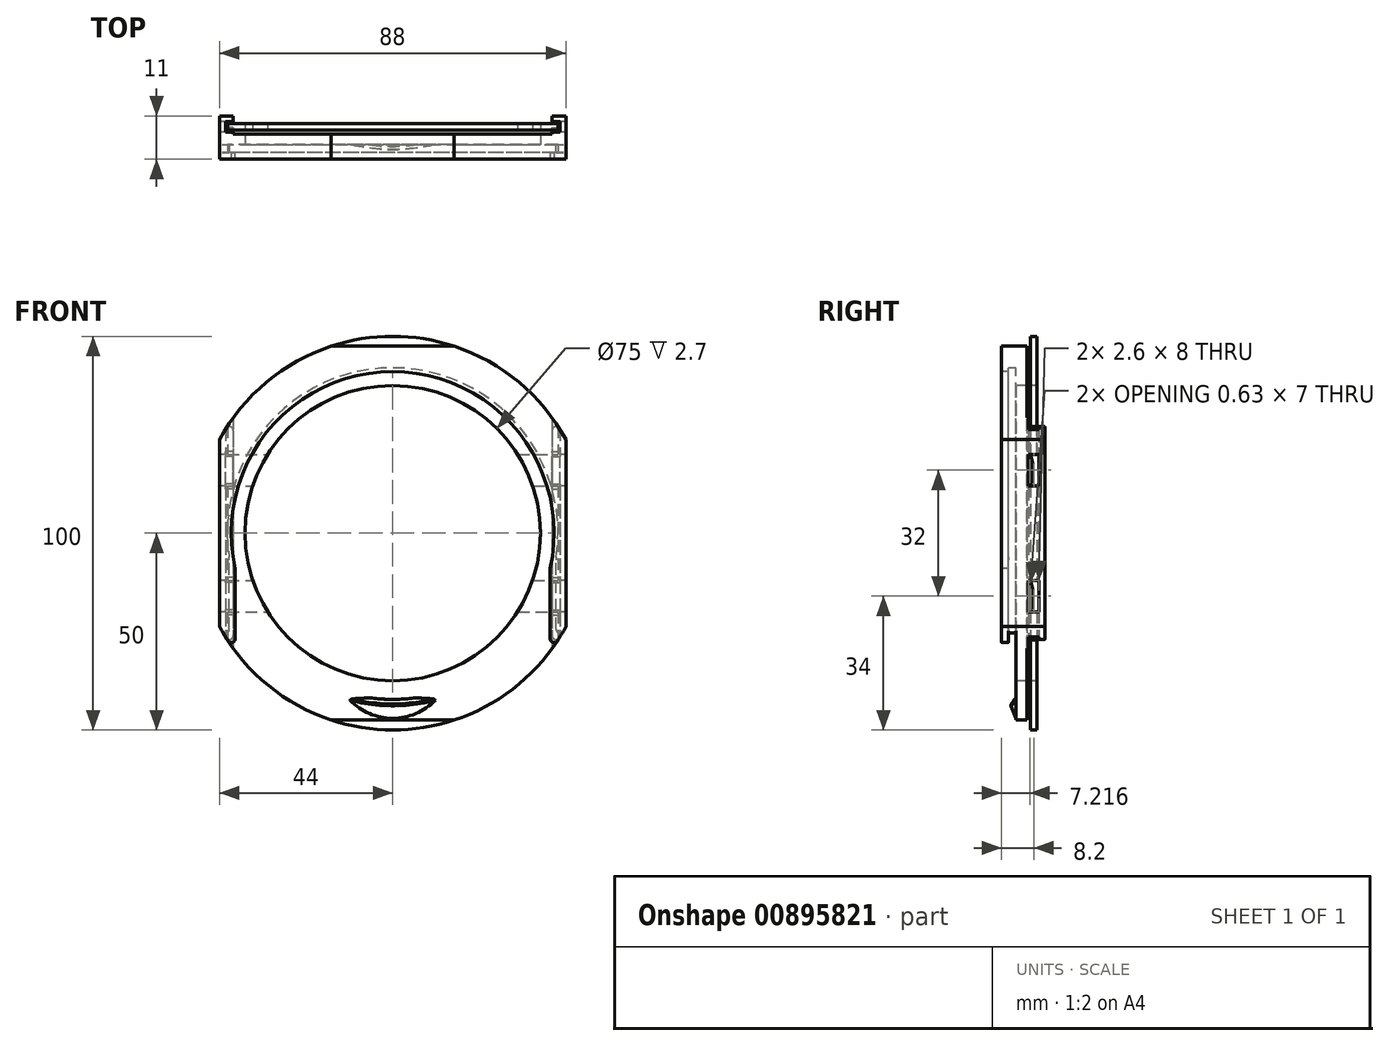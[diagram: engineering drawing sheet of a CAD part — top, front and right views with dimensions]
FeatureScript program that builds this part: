
annotation { "Feature Type Name" : "Feature", "Feature Type Description" : "" }
export const myFeature = defineFeature(function(context is Context, id is Id, definition is map)
    precondition{}
    {
        {
            var Q0;
            Q0=qCreatedBy(makeId("Front.planeOp"),FACE);
            var sketch = newSketch(context, id + "F0", { "sketchPlane" : qUnion([Q0])});
            skLineSegment(sketch, "E0.bottom", {"start": v(42, 50) * mm, "end": v(-42, 50) * mm});
            skLineSegment(sketch, "E0.top", {"start": v(42, -50) * mm, "end": v(-42, -50) * mm});
            skLineSegment(sketch, "E0.left", {"start": v(42, 50) * mm, "end": v(42, -50) * mm});
            skLineSegment(sketch, "E0.right", {"start": v(-42, 50) * mm, "end": v(-42, -50) * mm});
            skPoint(sketch, "E0.middle", {"position": v(0, 0) * mm});
            skSolve(sketch);
        }
        {
            var Q0;
            Q0=makeQuery(id+"F0.imprint","IMPRINT",FACE,{"disambiguationData":[TD([[makeQuery(id+"F0.imprint","IMPRINT",EDGE,{"derivedFrom":sQuery(id+"F0.wireOp",EDGE,"E0.bottom")}),1.0]])]});
            extrude(context, id + "F1", {"entities" : qUnion([Q0]), "depth" : .8 * mm, "offsetDistance" : 25 * mm, "hasSecondDirection" : true, "secondDirectionOppositeDirection" : true, "secondDirectionDepth" : .8 * mm});
        }
        {
            var Q0;
            Q0=qCreatedBy(makeId("Top.planeOp"),FACE);
            var sketch = newSketch(context, id + "F2", { "sketchPlane" : qUnion([Q0])});
            skLineSegment(sketch, "E1.0", {"start": v(42, 0.8) * mm, "end": v(-42, 0.8) * mm, "construction": true});
            skLineSegment(sketch, "E2.0", {"start": v(-42, -0.8) * mm, "end": v(-42, 0.8) * mm, "construction": true});
            skLineSegment(sketch, "E3.0", {"start": v(42, -0.8) * mm, "end": v(-42, -0.8) * mm, "construction": true});
            skLineSegment(sketch, "E4.0", {"start": v(42, -0.8) * mm, "end": v(42, 0.8) * mm, "construction": true});
            skLineSegment(sketch, "E5", {"start": v(-42.5, 1.3) * mm, "end": v(-42.5, -1.3) * mm});
            skLineSegment(sketch, "E6", {"start": v(-42.5, 1.3) * mm, "end": v(-40.5, 1.3) * mm});
            skLineSegment(sketch, "E7.MirrorCS", {"start": v(42.5, 1.3) * mm, "end": v(42.5, -1.3) * mm});
            skLineSegment(sketch, "E8.MirrorCS", {"start": v(42.5, 1.3) * mm, "end": v(40.5, 1.3) * mm});
            skLineSegment(sketch, "E9", {"start": v(-40.5, 1.3) * mm, "end": v(-40.5, 2.8) * mm});
            skLineSegment(sketch, "E10", {"start": v(-40.5, 2.8) * mm, "end": v(-44, 2.8) * mm});
            skLineSegment(sketch, "E11", {"start": v(-44, 2.8) * mm, "end": v(-44, -8.2) * mm});
            skLineSegment(sketch, "E12.MirrorCS", {"start": v(40.5, 1.3) * mm, "end": v(40.5, 2.8) * mm});
            skLineSegment(sketch, "E13.MirrorCS", {"start": v(40.5, 2.8) * mm, "end": v(44, 2.8) * mm});
            skLineSegment(sketch, "E14.MirrorCS", {"start": v(44, 2.8) * mm, "end": v(44, -8.2) * mm});
            skLineSegment(sketch, "E15", {"start": v(-44, -8.2) * mm, "end": v(44, -8.2) * mm});
            skLineSegment(sketch, "E16", {"start": v(-42.5, -1.3) * mm, "end": v(-40.5, -1.3) * mm});
            skLineSegment(sketch, "E17", {"start": v(-40.5, -1.3) * mm, "end": v(-40.5, -1.8) * mm});
            skLineSegment(sketch, "E18.MirrorCS", {"start": v(42.5, -1.3) * mm, "end": v(40.5, -1.3) * mm});
            skLineSegment(sketch, "E19.MirrorCS", {"start": v(40.5, -1.3) * mm, "end": v(40.5, -1.8) * mm});
            skLineSegment(sketch, "E20", {"start": v(40.5, -1.8) * mm, "end": v(-40.5, -1.8) * mm});
            skSolve(sketch);
        }
        {
            var Q0;
            Q0=qSketchRegion(id+"F2",true);
            extrude(context, id + "F3", {"entities" : qUnion([Q0]), "endBound" : BoundingType.SYMMETRIC, "depth" : 95 * mm, "offsetDistance" : 25 * mm});
        }
        {
            var Q0;
            Q0=qCreatedBy(makeId("Right.planeOp"),FACE);
            var sketch = newSketch(context, id + "F4", { "sketchPlane" : qUnion([Q0])});
            skLineSegment(sketch, "E21.top", {"start": v(3, 37.5) * mm, "end": v(-4.5, 37.5) * mm});
            skLineSegment(sketch, "E22", {"start": v(-4.5, 37.5) * mm, "end": v(-4.5, 42) * mm});
            skLineSegment(sketch, "E23", {"start": v(-4.5, 42) * mm, "end": v(-6.5, 42) * mm});
            skLineSegment(sketch, "E24", {"start": v(-6.5, 42) * mm, "end": v(-6.5, 41) * mm});
            skLineSegment(sketch, "E25", {"start": v(-6.5, 41) * mm, "end": v(-8.5, 41) * mm});
            skLineSegment(sketch, "E26", {"start": v(-8.5, 41) * mm, "end": v(-8.5, 0) * mm});
            skLineSegment(sketch, "E27", {"start": v(3, 37.5) * mm, "end": v(3, 0) * mm});
            skLineSegment(sketch, "E28", {"start": v(3, 0) * mm, "end": v(-8.5, 0) * mm});
            skSolve(sketch);
        }
        {
            var Q0;
            Q0=qSketchRegion(id+"F4",true);
            var Q1;
            Q1=sQuery(id+"F4.wireOp",EDGE,"E28");
            revolve(context, id + "F5", {"operationType" : NewBodyOperationType.REMOVE, "surfaceOperationType" : NewSurfaceOperationType.NEW, "entities" : qUnion([Q0]), "axis" : qUnion([Q1]), "revolveType" : RevolveType.FULL, "oppositeDirection" : true});
        }
        {
            var Q0;
            Q0=makeQuery(id+"F3.opExtrude","SWEPT_FACE",FACE,{"disambiguationData":[OSD([sQuery(id+"F2.wireOp",EDGE,"E15")])]});
            var sketch = newSketch(context, id + "F6", { "sketchPlane" : qUnion([Q0])});
            skLineSegment(sketch, "E29.0.0", {"start": v(-44, -47.5) * mm, "end": v(44, -47.5) * mm, "construction": true});
            skLineSegment(sketch, "E29.0.1", {"start": v(44, -47.5) * mm, "end": v(44, 47.5) * mm, "construction": true});
            skLineSegment(sketch, "E29.0.2", {"start": v(44, 47.5) * mm, "end": v(-44, 47.5) * mm, "construction": true});
            skLineSegment(sketch, "E29.0.3", {"start": v(-44, 47.5) * mm, "end": v(-44, -47.5) * mm, "construction": true});
            skLineSegment(sketch, "E30", {"start": v(-40, -9) * mm, "end": v(-40, -47.5) * mm});
            skLineSegment(sketch, "E31", {"start": v(40, -9) * mm, "end": v(40, -47.5) * mm});
            skArc(sketch, "E32", {"start": v(-40, -9) * mm, "mid": v(0, -41) * mm, "end": v(40, -9) * mm});
            skLineSegment(sketch, "E33", {"start": v(-40, -47.5) * mm, "end": v(40, -47.5) * mm});
            skSolve(sketch);
        }
        {
            var Q0;
            Q0=qSketchRegion(id+"F6",true);
            var Q1;
            Q1=makeQuery(id+"F5.boolean.opBoolean","COPY",FACE,{"derivedFrom":makeQuery(id+"F5.opRevolve","SWEPT_FACE",FACE,{"disambiguationData":[OSD([sQuery(id+"F4.wireOp",EDGE,"E22")])]})});
            extrude(context, id + "F7", {"entities" : qUnion([Q0]), "operationType" : NewBodyOperationType.REMOVE, "endBound" : BoundingType.UP_TO_SURFACE, "oppositeDirection" : true, "depth" : 25 * mm, "endBoundEntityFace" : qUnion([Q1]), "offsetDistance" : 25 * mm});
        }
        {
            var Q0;
            Q0=qCreatedBy(makeId("Front.planeOp"),FACE);
            var sketch = newSketch(context, id + "F8", { "sketchPlane" : qUnion([Q0])});
            skCircle(sketch, "E34", {"center": v(0, 0) * mm, "radius": 50 * mm});
            skCircle(sketch, "E35", {"center": v(0, 0) * mm, "radius": 70 * mm});
            skSolve(sketch);
        }
        {
            var Q0;
            Q0=qSketchRegion(id+"F8",true);
            extrude(context, id + "F9", {"entities" : qUnion([Q0]), "operationType" : NewBodyOperationType.REMOVE, "endBound" : BoundingType.SYMMETRIC, "oppositeDirection" : true, "depth" : 500 * mm, "offsetDistance" : 25 * mm});
        }
        {
            var Q0;
            Q0=qCreatedBy(makeId("Top.planeOp"),FACE);
            var sketch = newSketch(context, id + "F10", { "sketchPlane" : qUnion([Q0])});
            skLineSegment(sketch, "E36", {"start": v(-42, -4.5) * mm, "end": v(-42, -3.5) * mm, "construction": true});
            skLineSegment(sketch, "E37", {"start": v(42, -4.5) * mm, "end": v(42, -6.5) * mm, "construction": true});
            skLineSegment(sketch, "E38.bottom", {"start": v(-41.5, -4.5) * mm, "end": v(41.5, -4.5) * mm});
            skLineSegment(sketch, "E38.left", {"start": v(-41.5, -6.5) * mm, "end": v(-41.5, -4.5) * mm});
            skLineSegment(sketch, "E38.right", {"start": v(41.5, -6.5) * mm, "end": v(41.5, -4.5) * mm});
            skLineSegment(sketch, "E39.0.0", {"start": v(-15.61, -4.5) * mm, "end": v(15.61, -4.5) * mm});
            skLineSegment(sketch, "E39.0.1", {"start": v(15.61, -4.5) * mm, "end": v(40, -4.5) * mm});
            skLineSegment(sketch, "E39.0.3", {"start": v(42, -4.5) * mm, "end": v(-42, -4.5) * mm, "construction": true});
            skLineSegment(sketch, "E39.0.5", {"start": v(-40, -4.5) * mm, "end": v(-15.61, -4.5) * mm});
            skLineSegment(sketch, "E40.0", {"start": v(41, -6.5) * mm, "end": v(-41, -6.5) * mm, "construction": true});
            skLineSegment(sketch, "E41", {"start": v(-41.5, -6.5) * mm, "end": v(41.5, -6.5) * mm});
            skSolve(sketch);
        }
        {
            var Q0;
            Q0=qSketchRegion(id+"F10",true);
            extrude(context, id + "F11", {"entities" : qUnion([Q0]), "operationType" : NewBodyOperationType.REMOVE, "oppositeDirection" : true, "depth" : 50 * mm, "offsetDistance" : 25 * mm});
        }
        {
            var Q0;
            Q0=makeQuery(id+"F11.boolean.opBoolean","INTERSECT",EDGE,{"derivedFrom":[makeQuery(id+"F5.boolean.opBoolean","COPY",FACE,{"derivedFrom":makeQuery(id+"F5.opRevolve","SWEPT_FACE",FACE,{"disambiguationData":[OSD([sQuery(id+"F4.wireOp",EDGE,"E23")])]})}),makeQuery(id+"F11.opExtrude","SWEPT_FACE",FACE,{"disambiguationData":[OSD([sQuery(id+"F10.wireOp",EDGE,"E38.right")])]})]});
            var Q1;
            Q1=makeQuery(id+"F11.boolean.opBoolean","INTERSECT",EDGE,{"derivedFrom":[makeQuery(id+"F5.boolean.opBoolean","COPY",FACE,{"derivedFrom":makeQuery(id+"F5.opRevolve","SWEPT_FACE",FACE,{"disambiguationData":[OSD([sQuery(id+"F4.wireOp",EDGE,"E23")])]})}),makeQuery(id+"F11.opExtrude","SWEPT_FACE",FACE,{"disambiguationData":[OSD([sQuery(id+"F10.wireOp",EDGE,"E38.left")])]})]});
            fillet(context, id + "F12", {"entities" : qUnion([Q0, Q1]), "radius" : 5 * mm, "tangentPropagation" : true, "allowEdgeOverflow" : false});
        }
        {
            var Q0;
            {var subQ0=sQuery(id+"F2.wireOp",EDGE,"E16");var subQ1=sQuery(id+"F2.wireOp",EDGE,"E11");var subQ2=sQuery(id+"F2.wireOp",EDGE,"E10");var subQ3=sQuery(id+"F2.wireOp",EDGE,"E5");var subQ4=sQuery(id+"F2.wireOp",EDGE,"E15");var subQ5=sQuery(id+"F2.wireOp",EDGE,"E20");var subQ6=sQuery(id+"F2.wireOp",EDGE,"E17");var subQ7=sQuery(id+"F2.wireOp",EDGE,"E9");var subQ8=sQuery(id+"F2.wireOp",EDGE,"E6");Q0=makeQuery(id+"F11.boolean.opBoolean","INTERSECT",EDGE,{"derivedFrom":[makeQuery(id+"F9.boolean.opBoolean","COPY",FACE,{"disambiguationData":[TD([makeQuery(id+"F3.opExtrude","SWEPT_FACE",FACE,{"disambiguationData":[OSD([subQ3])]}),makeQuery(id+"F3.opExtrude","CAP_FACE",FACE,{"disambiguationData":[OSD([subQ3,subQ8,sQuery(id+"F2.wireOp",EDGE,"E7.MirrorCS"),sQuery(id+"F2.wireOp",EDGE,"E8.MirrorCS"),subQ7,subQ2,subQ1,sQuery(id+"F2.wireOp",EDGE,"E12.MirrorCS"),sQuery(id+"F2.wireOp",EDGE,"E13.MirrorCS"),sQuery(id+"F2.wireOp",EDGE,"E14.MirrorCS"),subQ4,subQ0,subQ6,sQuery(id+"F2.wireOp",EDGE,"E18.MirrorCS"),sQuery(id+"F2.wireOp",EDGE,"E19.MirrorCS"),subQ5])],"isStart":true}),makeQuery(id+"F3.opExtrude","SWEPT_FACE",FACE,{"disambiguationData":[OSD([subQ8])]}),makeQuery(id+"F3.opExtrude","SWEPT_FACE",FACE,{"disambiguationData":[OSD([subQ7])]}),makeQuery(id+"F3.opExtrude","SWEPT_FACE",FACE,{"disambiguationData":[OSD([subQ2])]}),makeQuery(id+"F3.opExtrude","SWEPT_FACE",FACE,{"disambiguationData":[OSD([subQ1])]}),makeQuery(id+"F3.opExtrude","SWEPT_FACE",FACE,{"disambiguationData":[OSD([subQ4])]}),makeQuery(id+"F3.opExtrude","SWEPT_FACE",FACE,{"disambiguationData":[OSD([subQ0])]}),makeQuery(id+"F3.opExtrude","SWEPT_FACE",FACE,{"disambiguationData":[OSD([subQ6])]}),makeQuery(id+"F3.opExtrude","SWEPT_FACE",FACE,{"disambiguationData":[OSD([subQ5])]}),makeQuery(id+"F5.boolean.opBoolean","COPY",FACE,{"derivedFrom":makeQuery(id+"F5.opRevolve","SWEPT_FACE",FACE,{"disambiguationData":[OSD([sQuery(id+"F4.wireOp",EDGE,"t31NqOFZ-bdFC-osZE-Ytuw-QL428Am0EnsE")])]})}),makeQuery(id+"F7.boolean.opBoolean","COPY",FACE,{"derivedFrom":makeQuery(id+"F7.opExtrude","SWEPT_FACE",FACE,{"disambiguationData":[OSD([sQuery(id+"F6.wireOp",EDGE,"E30")])]})})])],"derivedFrom":makeQuery(id+"F9.opExtrude","SWEPT_FACE",FACE,{"disambiguationData":[OSD([sQuery(id+"F8.wireOp",EDGE,"E34")])]})}),makeQuery(id+"F11.opExtrude","SWEPT_FACE",FACE,{"disambiguationData":[OSD([sQuery(id+"F10.wireOp",EDGE,"E38.left")])]})]});}
            var Q1;
            {var subQ0=sQuery(id+"F2.wireOp",EDGE,"E20");var subQ1=sQuery(id+"F2.wireOp",EDGE,"E14.MirrorCS");var subQ2=sQuery(id+"F2.wireOp",EDGE,"E13.MirrorCS");var subQ3=sQuery(id+"F2.wireOp",EDGE,"E15");var subQ4=sQuery(id+"F2.wireOp",EDGE,"E19.MirrorCS");var subQ5=sQuery(id+"F2.wireOp",EDGE,"E18.MirrorCS");var subQ6=sQuery(id+"F2.wireOp",EDGE,"E12.MirrorCS");var subQ7=sQuery(id+"F2.wireOp",EDGE,"E8.MirrorCS");var subQ8=sQuery(id+"F2.wireOp",EDGE,"E7.MirrorCS");Q1=makeQuery(id+"F11.boolean.opBoolean","INTERSECT",EDGE,{"derivedFrom":[makeQuery(id+"F9.boolean.opBoolean","COPY",FACE,{"disambiguationData":[TD([makeQuery(id+"F3.opExtrude","CAP_FACE",FACE,{"disambiguationData":[OSD([sQuery(id+"F2.wireOp",EDGE,"E5"),sQuery(id+"F2.wireOp",EDGE,"E6"),subQ8,subQ7,sQuery(id+"F2.wireOp",EDGE,"E9"),sQuery(id+"F2.wireOp",EDGE,"E10"),sQuery(id+"F2.wireOp",EDGE,"E11"),subQ6,subQ2,subQ1,subQ3,sQuery(id+"F2.wireOp",EDGE,"E16"),sQuery(id+"F2.wireOp",EDGE,"E17"),subQ5,subQ4,subQ0])],"isStart":true}),makeQuery(id+"F3.opExtrude","SWEPT_FACE",FACE,{"disambiguationData":[OSD([subQ8])]}),makeQuery(id+"F3.opExtrude","SWEPT_FACE",FACE,{"disambiguationData":[OSD([subQ7])]}),makeQuery(id+"F3.opExtrude","SWEPT_FACE",FACE,{"disambiguationData":[OSD([subQ6])]}),makeQuery(id+"F3.opExtrude","SWEPT_FACE",FACE,{"disambiguationData":[OSD([subQ2])]}),makeQuery(id+"F3.opExtrude","SWEPT_FACE",FACE,{"disambiguationData":[OSD([subQ1])]}),makeQuery(id+"F3.opExtrude","SWEPT_FACE",FACE,{"disambiguationData":[OSD([subQ3])]}),makeQuery(id+"F3.opExtrude","SWEPT_FACE",FACE,{"disambiguationData":[OSD([subQ5])]}),makeQuery(id+"F3.opExtrude","SWEPT_FACE",FACE,{"disambiguationData":[OSD([subQ4])]}),makeQuery(id+"F3.opExtrude","SWEPT_FACE",FACE,{"disambiguationData":[OSD([subQ0])]}),makeQuery(id+"F5.boolean.opBoolean","COPY",FACE,{"derivedFrom":makeQuery(id+"F5.opRevolve","SWEPT_FACE",FACE,{"disambiguationData":[OSD([sQuery(id+"F4.wireOp",EDGE,"t31NqOFZ-bdFC-osZE-Ytuw-QL428Am0EnsE")])]})}),makeQuery(id+"F7.boolean.opBoolean","COPY",FACE,{"derivedFrom":makeQuery(id+"F7.opExtrude","SWEPT_FACE",FACE,{"disambiguationData":[OSD([sQuery(id+"F6.wireOp",EDGE,"E31")])]})})])],"derivedFrom":makeQuery(id+"F9.opExtrude","SWEPT_FACE",FACE,{"disambiguationData":[OSD([sQuery(id+"F8.wireOp",EDGE,"E34")])]})}),makeQuery(id+"F11.opExtrude","SWEPT_FACE",FACE,{"disambiguationData":[OSD([sQuery(id+"F10.wireOp",EDGE,"E38.right")])]})]});}
            fillet(context, id + "F13", {"entities" : qUnion([Q0, Q1]), "radius" : 1 * mm, "tangentPropagation" : true, "allowEdgeOverflow" : false});
        }
        {
            var Q0;
            Q0=qCreatedBy(makeId("Right.planeOp"),FACE);
            var sketch = newSketch(context, id + "F14", { "sketchPlane" : qUnion([Q0])});
            skLineSegment(sketch, "E42.0.0", {"start": v(-8.2, 23.75) * mm, "end": v(2.8, 23.75) * mm, "construction": true});
            skLineSegment(sketch, "E42.0.1", {"start": v(2.8, 23.75) * mm, "end": v(2.8, -23.75) * mm, "construction": true});
            skLineSegment(sketch, "E42.0.2", {"start": v(-8.2, -23.75) * mm, "end": v(2.8, -23.75) * mm, "construction": true});
            skLineSegment(sketch, "E42.0.3", {"start": v(-8.2, -23.75) * mm, "end": v(-8.2, 23.75) * mm, "construction": true});
            skLineSegment(sketch, "E43.0", {"start": v(1.3, 26.34) * mm, "end": v(-1.3, 26.34) * mm, "construction": true});
            skLineSegment(sketch, "E44.0", {"start": v(-1.3, -26.34) * mm, "end": v(1.3, -26.34) * mm, "construction": true});
            skLineSegment(sketch, "E45.bottom", {"start": v(1.3, 20) * mm, "end": v(-1.3, 20) * mm});
            skLineSegment(sketch, "E45.top", {"start": v(1.3, 12) * mm, "end": v(-1.3, 12) * mm});
            skLineSegment(sketch, "E45.left", {"start": v(1.3, 20) * mm, "end": v(1.3, 12) * mm});
            skLineSegment(sketch, "E45.right", {"start": v(-1.3, 20) * mm, "end": v(-1.3, 12) * mm});
            skLineSegment(sketch, "E46.MirrorCS", {"start": v(1.3, -20) * mm, "end": v(-1.3, -20) * mm});
            skLineSegment(sketch, "E47.MirrorCS", {"start": v(-1.3, -20) * mm, "end": v(-1.3, -12) * mm});
            skLineSegment(sketch, "E48.MirrorCS", {"start": v(1.3, -12) * mm, "end": v(-1.3, -12) * mm});
            skLineSegment(sketch, "E49.MirrorCS", {"start": v(1.3, -20) * mm, "end": v(1.3, -12) * mm});
            skSolve(sketch);
        }
        {
            var Q0;
            Q0=makeQuery(id+"F14.imprint","IMPRINT",FACE,{"disambiguationData":[TD([[makeQuery(id+"F14.imprint","IMPRINT",EDGE,{"derivedFrom":sQuery(id+"F14.wireOp",EDGE,"E45.bottom")}),1.0]])]});
            var Q1;
            Q1=makeQuery(id+"F14.imprint","IMPRINT",FACE,{"disambiguationData":[TD([[makeQuery(id+"F14.imprint","IMPRINT",EDGE,{"derivedFrom":sQuery(id+"F14.wireOp",EDGE,"E46.MirrorCS")}),-1.0]])]});
            extrude(context, id + "F15", {"entities" : qUnion([Q0, Q1]), "operationType" : NewBodyOperationType.REMOVE, "endBound" : BoundingType.SYMMETRIC, "depth" : 100 * mm, "offsetDistance" : 25 * mm});
        }
        {
            var Q0;
            Q0=makeQuery(id+"F15.boolean.opBoolean","SPLIT",FACE,{"disambiguationData":[TD([makeQuery(id+"F15.opExtrude","SWEPT_FACE",FACE,{"disambiguationData":[OSD([sQuery(id+"F14.wireOp",EDGE,"E45.top")])]})])],"derivedFrom":makeQuery(id+"F3.opExtrude","SWEPT_FACE",FACE,{"disambiguationData":[OSD([sQuery(id+"F2.wireOp",EDGE,"E5")])]})});
            var sketch = newSketch(context, id + "F16", { "sketchPlane" : qUnion([Q0])});
            skLineSegment(sketch, "E50.0", {"start": v(-1.3, 20) * mm, "end": v(1.3, 20) * mm, "construction": true});
            skLineSegment(sketch, "E51.0", {"start": v(-1.3, 12) * mm, "end": v(1.3, 12) * mm, "construction": true});
            skArc(sketch, "E52", {"start": v(-1.3, 12.5) * mm, "mid": v(-0.67, 16) * mm, "end": v(-1.3, 19.5) * mm});
            skLineSegment(sketch, "E53", {"start": v(6.42, 16) * mm, "end": v(-9.93, 16) * mm, "construction": true});
            skArc(sketch, "E54.0", {"start": v(-1.3, 11.26) * mm, "mid": v(-0.17, 16) * mm, "end": v(-1.3, 20.74) * mm});
            skLineSegment(sketch, "E55", {"start": v(-1.3, 20.74) * mm, "end": v(-1.3, 19.5) * mm});
            skLineSegment(sketch, "E56", {"start": v(-1.3, 12.5) * mm, "end": v(-1.3, 11.26) * mm});
            skSolve(sketch);
        }
        {
            var Q0;
            {var subQ0=sQuery(id+"F16.wireOp",EDGE,"E55");Q0=makeQuery(id+"F16.imprint","IMPRINT",FACE,{"disambiguationData":[TD([[makeQuery(id+"F16.imprint","IMPRINT",EDGE,{"derivedFrom":subQ0}),1.0]])]});}
            var Q1;
            {var subQ0=sQuery(id+"F16.wireOp",EDGE,"E56");Q1=makeQuery(id+"F16.imprint","IMPRINT",FACE,{"disambiguationData":[TD([[makeQuery(id+"F16.imprint","IMPRINT",EDGE,{"derivedFrom":subQ0}),1.0]])]});}
            extrude(context, id + "F17", {"entities" : qUnion([Q0, Q1]), "depth" : 2 * mm, "offsetDistance" : 25 * mm});
        }
        {
            var Q0;
            Q0=makeQuery(id+"F17.opExtrude","SWEPT_BODY",BODY,{"disambiguationData":[OSD([sQuery(id+"F16.wireOp",EDGE,"E52"),sQuery(id+"F16.wireOp",EDGE,"E54.0"),sQuery(id+"F16.wireOp",EDGE,"E55"),sQuery(id+"F16.wireOp",EDGE,"E56")])]});
            var Q1;
            Q1=qCreatedBy(makeId("Right.planeOp"),FACE);
            mirror(context, id + "F18", {"entities" : qUnion([Q0]), "mirrorPlane" : qUnion([Q1])});
        }
        {
            var Q0;
            Q0=makeQuery(id+"F18.opPattern","COPY",BODY,{"derivedFrom":makeQuery(id+"F17.opExtrude","SWEPT_BODY",BODY,{"disambiguationData":[OSD([sQuery(id+"F16.wireOp",EDGE,"E52"),sQuery(id+"F16.wireOp",EDGE,"E54.0"),sQuery(id+"F16.wireOp",EDGE,"E55"),sQuery(id+"F16.wireOp",EDGE,"E56")])]}),"instanceName":"1"});
            var Q1;
            Q1=makeQuery(id+"F17.opExtrude","SWEPT_BODY",BODY,{"disambiguationData":[OSD([sQuery(id+"F16.wireOp",EDGE,"E52"),sQuery(id+"F16.wireOp",EDGE,"E54.0"),sQuery(id+"F16.wireOp",EDGE,"E55"),sQuery(id+"F16.wireOp",EDGE,"E56")])]});
            var Q2;
            Q2=qCreatedBy(makeId("Top.planeOp"),FACE);
            mirror(context, id + "F19", {"operationType" : NewBodyOperationType.ADD, "entities" : qUnion([Q0, Q1]), "mirrorPlane" : qUnion([Q2])});
        }
        {
            var Q0;
            Q0=makeQuery(id+"F9.boolean.opBoolean","INTERSECT",EDGE,{"derivedFrom":[makeQuery(id+"F7.boolean.opBoolean","COPY",FACE,{"derivedFrom":makeQuery(id+"F7.opExtrude","SWEPT_FACE",FACE,{"disambiguationData":[OSD([sQuery(id+"F6.wireOp",EDGE,"E31")])]})}),makeQuery(id+"F9.opExtrude","SWEPT_FACE",FACE,{"disambiguationData":[OSD([sQuery(id+"F8.wireOp",EDGE,"E34")])]})]});
            var Q1;
            Q1=makeQuery(id+"F9.boolean.opBoolean","INTERSECT",EDGE,{"derivedFrom":[makeQuery(id+"F7.boolean.opBoolean","COPY",FACE,{"derivedFrom":makeQuery(id+"F7.opExtrude","SWEPT_FACE",FACE,{"disambiguationData":[OSD([sQuery(id+"F6.wireOp",EDGE,"E30")])]})}),makeQuery(id+"F9.opExtrude","SWEPT_FACE",FACE,{"disambiguationData":[OSD([sQuery(id+"F8.wireOp",EDGE,"E34")])]})]});
            var Q2;
            Q2=makeQuery(id+"F9.boolean.opBoolean","INTERSECT",EDGE,{"disambiguationData":[OD(1.0)],"derivedFrom":[makeQuery(id+"F3.opExtrude","SWEPT_FACE",FACE,{"disambiguationData":[OSD([sQuery(id+"F2.wireOp",EDGE,"E12.MirrorCS")])]}),makeQuery(id+"F9.opExtrude","SWEPT_FACE",FACE,{"disambiguationData":[OSD([sQuery(id+"F8.wireOp",EDGE,"E34")])]})]});
            var Q3;
            Q3=makeQuery(id+"F9.boolean.opBoolean","INTERSECT",EDGE,{"disambiguationData":[OD(1.0)],"derivedFrom":[makeQuery(id+"F3.opExtrude","SWEPT_FACE",FACE,{"disambiguationData":[OSD([sQuery(id+"F2.wireOp",EDGE,"E9")])]}),makeQuery(id+"F9.opExtrude","SWEPT_FACE",FACE,{"disambiguationData":[OSD([sQuery(id+"F8.wireOp",EDGE,"E34")])]})]});
            var Q4;
            Q4=makeQuery(id+"F9.boolean.opBoolean","INTERSECT",EDGE,{"disambiguationData":[OD(0.0)],"derivedFrom":[makeQuery(id+"F3.opExtrude","SWEPT_FACE",FACE,{"disambiguationData":[OSD([sQuery(id+"F2.wireOp",EDGE,"E9")])]}),makeQuery(id+"F9.opExtrude","SWEPT_FACE",FACE,{"disambiguationData":[OSD([sQuery(id+"F8.wireOp",EDGE,"E34")])]})]});
            var Q5;
            Q5=makeQuery(id+"F9.boolean.opBoolean","INTERSECT",EDGE,{"disambiguationData":[OD(0.0)],"derivedFrom":[makeQuery(id+"F3.opExtrude","SWEPT_FACE",FACE,{"disambiguationData":[OSD([sQuery(id+"F2.wireOp",EDGE,"E12.MirrorCS")])]}),makeQuery(id+"F9.opExtrude","SWEPT_FACE",FACE,{"disambiguationData":[OSD([sQuery(id+"F8.wireOp",EDGE,"E34")])]})]});
            fillet(context, id + "F20", {"entities" : qUnion([Q0, Q1, Q2, Q3, Q4, Q5]), "radius" : 1 * mm, "tangentPropagation" : true, "allowEdgeOverflow" : false});
        }
        {
            var Q0;
            Q0=makeQuery(id+"F11.boolean.opBoolean","MERGE",FACE,{"derivedFrom":[makeQuery(id+"F7.boolean.opBoolean","MERGE",FACE,{"derivedFrom":[makeQuery(id+"F5.boolean.opBoolean","COPY",FACE,{"derivedFrom":makeQuery(id+"F5.opRevolve","SWEPT_FACE",FACE,{"disambiguationData":[OSD([sQuery(id+"F4.wireOp",EDGE,"E22")])]})})],"fromTools":[makeQuery(id+"F7.opExtrude","CAP_FACE",FACE,{"disambiguationData":[OSD([sQuery(id+"F6.wireOp",EDGE,"E30"),sQuery(id+"F6.wireOp",EDGE,"E31"),sQuery(id+"F6.wireOp",EDGE,"E32"),sQuery(id+"F6.wireOp",EDGE,"E33")])],"isStart":false})]})],"fromTools":[makeQuery(id+"F11.opExtrude","SWEPT_FACE",FACE,{"disambiguationData":[OSD([sQuery(id+"F10.wireOp",EDGE,"E38.bottom"),sQuery(id+"F10.wireOp",EDGE,"E39.0.0"),sQuery(id+"F10.wireOp",EDGE,"E39.0.1"),sQuery(id+"F10.wireOp",EDGE,"E39.0.5")])]})]});
            var sketch = newSketch(context, id + "F21", { "sketchPlane" : qUnion([Q0])});
            skArc(sketch, "E57", {"start": v(-12.5, -40.36) * mm, "mid": v(0, -42.25) * mm, "end": v(12.5, -40.36) * mm});
            skArc(sketch, "E58", {"start": v(-12.5, -40.36) * mm, "mid": v(0, -47.07) * mm, "end": v(12.5, -40.36) * mm});
            skSolve(sketch);
        }
        {
            var Q0;
            Q0=makeQuery(id+"F21.imprint","IMPRINT",FACE,{"disambiguationData":[TD([[makeQuery(id+"F21.imprint","IMPRINT",EDGE,{"derivedFrom":sQuery(id+"F21.wireOp",EDGE,"E57")}),-1.0]])]});
            extrude(context, id + "F22", {"entities" : qUnion([Q0]), "operationType" : NewBodyOperationType.ADD, "depth" : 2 * mm, "offsetDistance" : 25 * mm});
        }
        {
            var Q0;
            Q0=makeQuery(id+"F22.opExtrude","CAP_EDGE",EDGE,{"disambiguationData":[OSD([sQuery(id+"F21.wireOp",EDGE,"E58")])],"isStart":false});
            chamfer(context, id + "F23", {"entities" : qUnion([Q0]), "chamferType" : ChamferType.TWO_OFFSETS, "width1" : 5 * mm, "oppositeDirection" : false, "width2" : 2 * mm, "tangentPropagation" : true});
        }
        {
            var Q0;
            Q0=makeQuery(id+"F23.opChamfer","BLEND_EDGE",EDGE,{"blendedFrom":[makeQuery(id+"F22.opExtrude","CAP_EDGE",EDGE,{"disambiguationData":[OSD([sQuery(id+"F21.wireOp",EDGE,"E58")])],"isStart":false}),makeQuery(id+"F22.opExtrude","SWEPT_FACE",FACE,{"disambiguationData":[OSD([sQuery(id+"F21.wireOp",EDGE,"E57")])]})],"blendedInto":[makeQuery(id+"F22.opExtrude","SWEPT_FACE",FACE,{"disambiguationData":[OSD([sQuery(id+"F21.wireOp",EDGE,"E57")])]})]});
            chamfer(context, id + "F24", {"entities" : qUnion([Q0]), "width" : 1 * mm, "tangentPropagation" : true});
        }
        {
            var Q0;
            {var subQ0=sQuery(id+"F21.wireOp",EDGE,"E58");Q0=makeQuery(id+"F24.opChamfer","BLEND_EDGE",EDGE,{"blendedFrom":[makeQuery(id+"F23.opChamfer","BLEND_EDGE",EDGE,{"blendedFrom":[makeQuery(id+"F22.opExtrude","CAP_EDGE",EDGE,{"disambiguationData":[OSD([subQ0])],"isStart":false}),makeQuery(id+"F22.opExtrude","SWEPT_FACE",FACE,{"disambiguationData":[OSD([sQuery(id+"F21.wireOp",EDGE,"E57")])]})],"blendedInto":[makeQuery(id+"F22.opExtrude","SWEPT_FACE",FACE,{"disambiguationData":[OSD([sQuery(id+"F21.wireOp",EDGE,"E57")])]})]}),makeQuery(id+"F23.opChamfer","BLEND_FACE",FACE,{"disambiguationData":[OSD([subQ0])]})],"blendedInto":[makeQuery(id+"F23.opChamfer","BLEND_FACE",FACE,{"disambiguationData":[OSD([subQ0])]})]});}
            chamfer(context, id + "F25", {"entities" : qUnion([Q0]), "width" : .5 * mm, "tangentPropagation" : true});
        }
    });
